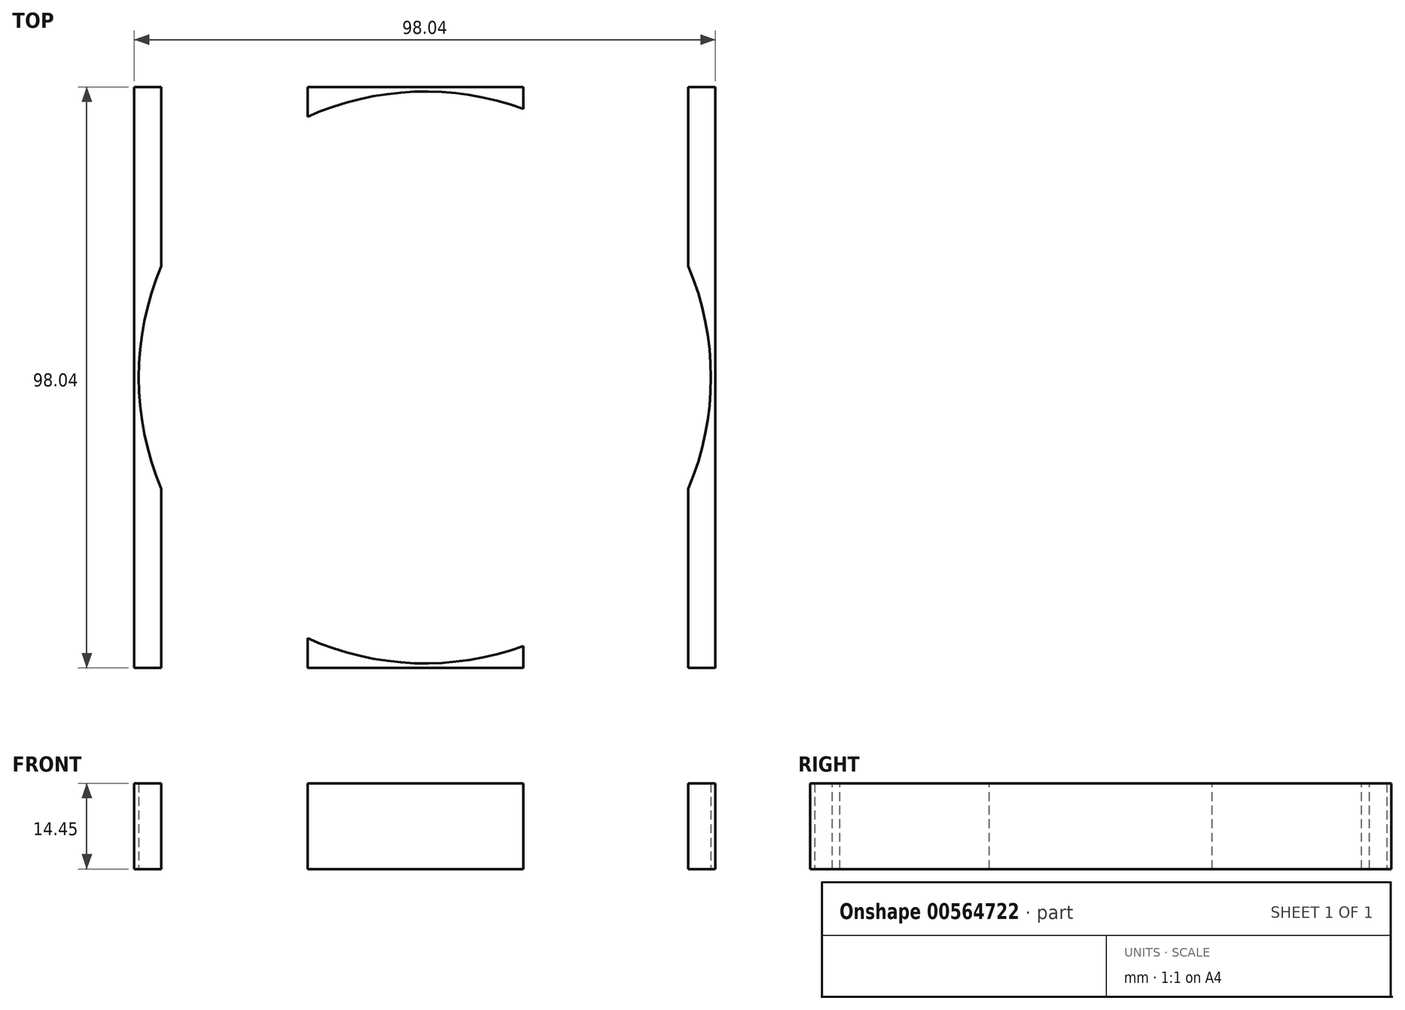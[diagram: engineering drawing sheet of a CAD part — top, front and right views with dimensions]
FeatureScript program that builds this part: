
annotation { "Feature Type Name" : "Feature", "Feature Type Description" : "" }
export const myFeature = defineFeature(function(context is Context, id is Id, definition is map)
    precondition{}
    {
        {
            var Q0;
            Q0=qCreatedBy(makeId("Top.planeOp"),FACE);
            var sketch = newSketch(context, id + "F0", { "sketchPlane" : qUnion([Q0])});
            skPoint(sketch, "E0.middle", {"position": v(0, 0) * mm});
            skLineSegment(sketch, "E1.bottom", {"start": v(-49.02, -49.02) * mm, "end": v(49.02, -49.02) * mm});
            skLineSegment(sketch, "E1.top", {"start": v(-49.02, 49.02) * mm, "end": v(49.02, 49.02) * mm});
            skLineSegment(sketch, "E1.left", {"start": v(-49.02, -49.02) * mm, "end": v(-49.02, 49.02) * mm});
            skLineSegment(sketch, "E1.right", {"start": v(49.02, -49.02) * mm, "end": v(49.02, 49.02) * mm});
            skSolve(sketch);
        }
        {
            var Q0;
            Q0=makeQuery(id+"F0.imprint","IMPRINT",FACE,{"disambiguationData":[TD([[makeQuery(id+"F0.imprint","IMPRINT",EDGE,{"derivedFrom":sQuery(id+"F0.wireOp",EDGE,"E1.bottom")}),1.0]])]});
            extrude(context, id + "F1", {"entities" : qUnion([Q0]), "depth" : 15.24 * mm, "offsetDistance" : 25.4 * mm});
        }
        {
            var Q0;
            Q0=makeQuery(id+"F1.opExtrude","CAP_FACE",FACE,{"disambiguationData":[OSD([sQuery(id+"F0.wireOp",EDGE,"E1.bottom"),sQuery(id+"F0.wireOp",EDGE,"E1.top"),sQuery(id+"F0.wireOp",EDGE,"E1.left"),sQuery(id+"F0.wireOp",EDGE,"E1.right")])],"isStart":false});
            var sketch = newSketch(context, id + "F2", { "sketchPlane" : qUnion([Q0])});
            skLineSegment(sketch, "E2", {"start": v(0, 49.02) * mm, "end": v(0, -49.02) * mm, "construction": true});
            skLineSegment(sketch, "E3", {"start": v(-25.4, 49.02) * mm, "end": v(-25.4, -49.02) * mm});
            skLineSegment(sketch, "E4", {"start": v(25.4, 49.02) * mm, "end": v(25.4, -49.02) * mm});
            skLineSegment(sketch, "E5", {"start": v(-22.23, 49.02) * mm, "end": v(-22.22, -49.02) * mm});
            skLineSegment(sketch, "E6", {"start": v(22.22, 49.02) * mm, "end": v(22.23, -49.02) * mm});
            skLineSegment(sketch, "E7", {"start": v(-44.45, 49.02) * mm, "end": v(-44.45, -49.02) * mm});
            skLineSegment(sketch, "E8", {"start": v(44.45, 49.02) * mm, "end": v(44.45, -49.02) * mm});
            skPoint(sketch, "E9", {"position": v(0, 0) * mm});
            skSolve(sketch);
        }
        {
            var Q0;
            Q0=sQuery(id+"F2.wireOp",VERTEX,"E9");
            var Q1;
            Q1=makeQuery(id+"F1.opExtrude","SWEPT_BODY",BODY,{"disambiguationData":[OSD([sQuery(id+"F0.wireOp",EDGE,"E1.bottom"),sQuery(id+"F0.wireOp",EDGE,"E1.top"),sQuery(id+"F0.wireOp",EDGE,"E1.left"),sQuery(id+"F0.wireOp",EDGE,"E1.right")])]});
            hole(context, id + "F3", {"style" : HoleStyle.SIMPLE, "endStyle" : HoleEndStyle.THROUGH, "holeDiameter" : 12.7 * mm, "isTappedThrough" : true, "tappedDepth" : 12.7 * mm, "tapClearance" : 3, "locations" : qUnion([Q0]), "scope" : qUnion([Q1])});
        }
        {
            var Q0;
            {var subQ0=sQuery(id+"F2.wireOp",EDGE,"E7");Q0=makeQuery(id+"F2.imprint","IMPRINT",FACE,{"disambiguationData":[TD([[makeQuery(id+"F2.imprint","IMPRINT",EDGE,{"derivedFrom":subQ0}),-1.0]])]});}
            var Q1;
            {var subQ0=sQuery(id+"F2.wireOp",EDGE,"E8");Q1=makeQuery(id+"F2.imprint","IMPRINT",FACE,{"disambiguationData":[TD([[makeQuery(id+"F2.imprint","IMPRINT",EDGE,{"derivedFrom":subQ0}),1.0]])]});}
            var Q2;
            {var subQ0=sQuery(id+"F2.wireOp",EDGE,"E5");Q2=makeQuery(id+"F2.imprint","IMPRINT",FACE,{"disambiguationData":[TD([[makeQuery(id+"F2.imprint","IMPRINT",EDGE,{"derivedFrom":subQ0}),1.0]])]});}
            extrude(context, id + "F4", {"entities" : qUnion([Q0, Q1, Q2]), "operationType" : NewBodyOperationType.REMOVE, "oppositeDirection" : true, "depth" : 0.79 * mm, "offsetDistance" : 25.4 * mm});
        }
        {
            var Q0;
            Q0=qCreatedBy(makeId("Front.planeOp"),FACE);
            var sketch = newSketch(context, id + "F5", { "sketchPlane" : qUnion([Q0])});
            skLineSegment(sketch, "E10", {"start": v(-44.45, 30.48) * mm, "end": v(-19.78, 30.48) * mm});
            skLineSegment(sketch, "E11", {"start": v(44.45, 15.24) * mm, "end": v(44.45, 30.48) * mm});
            skLineSegment(sketch, "E12", {"start": v(-44.45, 15.24) * mm, "end": v(-44.45, 30.48) * mm});
            skLineSegment(sketch, "E13", {"start": v(25.4, 15.24) * mm, "end": v(16.6, 30.48) * mm});
            skLineSegment(sketch, "E14", {"start": v(16.6, 30.48) * mm, "end": v(44.45, 30.48) * mm});
            skLineSegment(sketch, "E15", {"start": v(-44.45, 15.24) * mm, "end": v(-28.58, 15.24) * mm});
            skLineSegment(sketch, "E16", {"start": v(-19.78, 30.48) * mm, "end": v(-28.58, 15.24) * mm});
            skLineSegment(sketch, "E17", {"start": v(-19.78, 30.48) * mm, "end": v(16.6, 30.48) * mm, "construction": true});
            skLineSegment(sketch, "E18", {"start": v(-44.45, 22.86) * mm, "end": v(44.45, 22.86) * mm, "construction": true});
            skPoint(sketch, "E19", {"position": v(0, 22.86) * mm});
            skCircle(sketch, "E20", {"center": v(0, 22.86) * mm, "radius": 4.76 * mm, "construction": true});
            skLineSegment(sketch, "E21", {"start": v(-7.94, 30.48) * mm, "end": v(-7.94, 15.24) * mm, "construction": true});
            skLineSegment(sketch, "E22", {"start": v(7.94, 30.48) * mm, "end": v(7.94, 15.24) * mm, "construction": true});
            skLineSegment(sketch, "E23", {"start": v(0, 30.48) * mm, "end": v(0, 15.24) * mm, "construction": true});
            skLineSegment(sketch, "E24", {"start": v(44.45, 15.24) * mm, "end": v(25.4, 15.24) * mm});
            skLineSegment(sketch, "E25", {"start": v(-28.58, 15.24) * mm, "end": v(25.4, 15.24) * mm, "construction": true});
            skSolve(sketch);
        }
        {
            var Q0;
            Q0=makeQuery(id+"F5.imprint","IMPRINT",FACE,{"disambiguationData":[TD([[makeQuery(id+"F5.imprint","IMPRINT",EDGE,{"derivedFrom":sQuery(id+"F5.wireOp",EDGE,"E10")}),-1.0]])]});
            var Q1;
            Q1=makeQuery(id+"F5.imprint","IMPRINT",FACE,{"disambiguationData":[TD([[makeQuery(id+"F5.imprint","IMPRINT",EDGE,{"derivedFrom":sQuery(id+"F5.wireOp",EDGE,"E11")}),1.0]])]});
            extrude(context, id + "F6", {"entities" : qUnion([Q0, Q1]), "depth" : 50.8 * mm, "offsetDistance" : 25.4 * mm, "hasSecondDirection" : true, "secondDirectionOppositeDirection" : true, "secondDirectionDepth" : 50.8 * mm});
        }
        {
            var Q0;
            Q0=makeQuery(id+"F6.opExtrude","SWEPT_FACE",FACE,{"disambiguationData":[OSD([sQuery(id+"F5.wireOp",EDGE,"E10")])]});
            var sketch = newSketch(context, id + "F7", { "sketchPlane" : qUnion([Q0])});
            skCircle(sketch, "E26.0", {"center": v(0, 0) * mm, "radius": 6.35 * mm});
            skCircle(sketch, "E27", {"center": v(0, 0) * mm, "radius": 48.26 * mm});
            skSolve(sketch);
        }
        {
            var Q0;
            {var subQ1=sQuery(id+"F5.wireOp",EDGE,"E10");var subQ6=makeQuery(id+"F6.opExtrude","CAP_EDGE",EDGE,{"disambiguationData":[OSD([subQ1])],"isStart":true});Q0=makeQuery(id+"F7.imprint","IMPRINT",FACE,{"disambiguationData":[TD([[makeQuery(id+"F7.imprint","IMPRINT",EDGE,{"derivedFrom":subQ6}),-1.0]])]});}
            var Q1;
            {var subQ1=sQuery(id+"F5.wireOp",EDGE,"E10");var subQ6=makeQuery(id+"F6.opExtrude","CAP_EDGE",EDGE,{"disambiguationData":[OSD([subQ1])],"isStart":false});Q1=makeQuery(id+"F7.imprint","IMPRINT",FACE,{"disambiguationData":[TD([[makeQuery(id+"F7.imprint","IMPRINT",EDGE,{"derivedFrom":subQ6}),1.0]])]});}
            extrude(context, id + "F8", {"entities" : qUnion([Q0, Q1]), "operationType" : NewBodyOperationType.REMOVE, "endBound" : BoundingType.THROUGH_ALL, "oppositeDirection" : true, "depth" : 25.4 * mm, "offsetDistance" : 25.4 * mm});
        }
        {
            var Q0;
            Q0=makeQuery(id+"F6.opExtrude","SWEPT_FACE",FACE,{"disambiguationData":[OSD([sQuery(id+"F5.wireOp",EDGE,"E14")])]});
            var sketch = newSketch(context, id + "F9", { "sketchPlane" : qUnion([Q0])});
            skCircle(sketch, "E28", {"center": v(0, 0) * mm, "radius": 48.26 * mm});
            skSolve(sketch);
        }
        {
            var Q0;
            {var subQ1=sQuery(id+"F5.wireOp",EDGE,"E14");var subQ6=makeQuery(id+"F6.opExtrude","CAP_EDGE",EDGE,{"disambiguationData":[OSD([subQ1])],"isStart":true});Q0=makeQuery(id+"F9.imprint","IMPRINT",FACE,{"disambiguationData":[TD([[makeQuery(id+"F9.imprint","IMPRINT",EDGE,{"derivedFrom":subQ6}),-1.0]])]});}
            var Q1;
            {var subQ1=sQuery(id+"F5.wireOp",EDGE,"E14");var subQ6=makeQuery(id+"F6.opExtrude","CAP_EDGE",EDGE,{"disambiguationData":[OSD([subQ1])],"isStart":false});Q1=makeQuery(id+"F9.imprint","IMPRINT",FACE,{"disambiguationData":[TD([[makeQuery(id+"F9.imprint","IMPRINT",EDGE,{"derivedFrom":subQ6}),1.0]])]});}
            extrude(context, id + "F10", {"entities" : qUnion([Q0, Q1]), "operationType" : NewBodyOperationType.REMOVE, "endBound" : BoundingType.THROUGH_ALL, "oppositeDirection" : true, "depth" : 25.4 * mm, "offsetDistance" : 25.4 * mm});
        }
        {
            var Q0;
            Q0=makeQuery(id+"F1.opExtrude","CAP_FACE",FACE,{"disambiguationData":[OSD([sQuery(id+"F0.wireOp",EDGE,"E1.bottom"),sQuery(id+"F0.wireOp",EDGE,"E1.top"),sQuery(id+"F0.wireOp",EDGE,"E1.left"),sQuery(id+"F0.wireOp",EDGE,"E1.right")])],"isStart":true});
            var sketch = newSketch(context, id + "F11", { "sketchPlane" : qUnion([Q0])});
            skCircle(sketch, "E29", {"center": v(0, 0) * mm, "radius": 48.26 * mm});
            skSolve(sketch);
        }
        {
            var Q0;
            Q0=makeQuery(id+"F11.imprint","IMPRINT",FACE,{"disambiguationData":[TD([[makeQuery(id+"F11.imprint","IMPRINT",EDGE,{"derivedFrom":sQuery(id+"F11.wireOp",EDGE,"E29")}),-1.0]])]});
            extrude(context, id + "F12", {"entities" : qUnion([Q0]), "operationType" : NewBodyOperationType.REMOVE, "endBound" : BoundingType.THROUGH_ALL, "oppositeDirection" : true, "depth" : 25.4 * mm, "offsetDistance" : 25.4 * mm});
        }
    });
